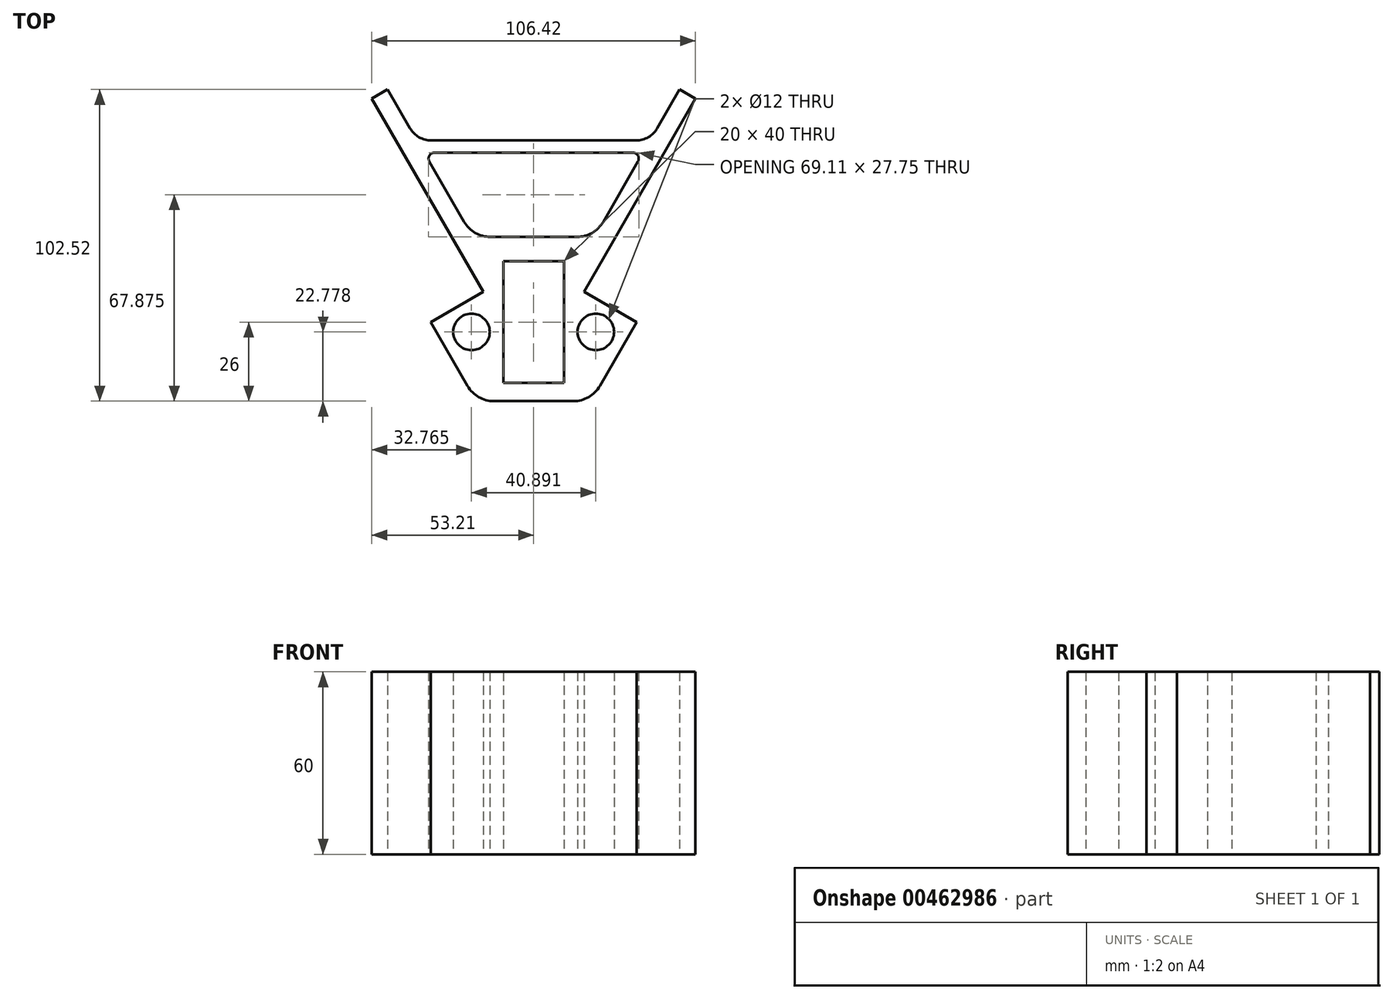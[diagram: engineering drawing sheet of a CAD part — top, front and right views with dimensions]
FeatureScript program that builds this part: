
annotation { "Feature Type Name" : "Feature", "Feature Type Description" : "" }
export const myFeature = defineFeature(function(context is Context, id is Id, definition is map)
    precondition{}
    {
        {
            var Q0;
            Q0=qCreatedBy(makeId("Top.planeOp"),FACE);
            var sketch = newSketch(context, id + "F0", { "sketchPlane" : qUnion([Q0])});
            skLineSegment(sketch, "E0.bottom", {"start": v(53.2, 49.76) * mm, "end": v(-53.2, 49.76) * mm, "construction": true});
            skLineSegment(sketch, "E0.top", {"start": v(53.2, -49.76) * mm, "end": v(-53.2, -49.76) * mm, "construction": true});
            skLineSegment(sketch, "E0.left", {"start": v(53.2, 49.76) * mm, "end": v(53.2, -49.76) * mm, "construction": true});
            skLineSegment(sketch, "E0.right", {"start": v(-53.2, 49.76) * mm, "end": v(-53.2, -49.76) * mm, "construction": true});
            skPoint(sketch, "E0.middle", {"position": v(0, 0) * mm});
            skLineSegment(sketch, "E1", {"start": v(-53.2, 49.76) * mm, "end": v(-16.53, -13.75) * mm});
            skLineSegment(sketch, "E2", {"start": v(53.2, 49.76) * mm, "end": v(16.54, -13.75) * mm});
            skLineSegment(sketch, "E3", {"start": v(-53.2, 49.76) * mm, "end": v(-48, 52.76) * mm});
            skLineSegment(sketch, "E4", {"start": v(-48, 52.76) * mm, "end": v(-40.64, 40) * mm});
            skLineSegment(sketch, "E5", {"start": v(53.2, 49.76) * mm, "end": v(48, 52.76) * mm});
            skLineSegment(sketch, "E6", {"start": v(48, 52.76) * mm, "end": v(40.64, 40) * mm});
            skLineSegment(sketch, "E7", {"start": v(16.54, -13.75) * mm, "end": v(33.86, -23.75) * mm});
            skLineSegment(sketch, "E8", {"start": v(33.86, -23.75) * mm, "end": v(21.73, -44.76) * mm});
            skLineSegment(sketch, "E9", {"start": v(-16.53, -13.75) * mm, "end": v(-33.86, -23.75) * mm});
            skLineSegment(sketch, "E10", {"start": v(-33.86, -23.75) * mm, "end": v(-21.73, -44.76) * mm});
            skLineSegment(sketch, "E11", {"start": v(-13.07, -49.76) * mm, "end": v(13.07, -49.76) * mm});
            skPoint(sketch, "E12.visualSharp", {"position": v(-18.84, -49.76) * mm});
            skArc(sketch, "E12.filletArc", {"start": v(-21.73, -44.76) * mm, "mid": v(-18.07, -48.42) * mm, "end": v(-13.07, -49.76) * mm});
            skPoint(sketch, "E13.visualSharp", {"position": v(18.84, -49.76) * mm});
            skArc(sketch, "E13.filletArc", {"start": v(13.07, -49.76) * mm, "mid": v(18.07, -48.42) * mm, "end": v(21.73, -44.76) * mm});
            skLineSegment(sketch, "E14.bottom", {"start": v(10, -43.76) * mm, "end": v(-10, -43.76) * mm});
            skLineSegment(sketch, "E14.top", {"start": v(10, -3.76) * mm, "end": v(-10, -3.76) * mm});
            skLineSegment(sketch, "E14.left", {"start": v(10, -43.76) * mm, "end": v(10, -3.76) * mm});
            skLineSegment(sketch, "E14.right", {"start": v(-10, -43.76) * mm, "end": v(-10, -3.76) * mm});
            skPoint(sketch, "E14.middle", {"position": v(0, -23.76) * mm});
            skLineSegment(sketch, "E15", {"start": v(14.22, 4.24) * mm, "end": v(-14.22, 4.24) * mm});
            skPoint(sketch, "E16.orphan", {"position": v(-19.1, 2.67) * mm});
            skPoint(sketch, "E17.orphan", {"position": v(19.1, 2.67) * mm});
            skPoint(sketch, "E18.visualSharp", {"position": v(-20, 4.24) * mm});
            skArc(sketch, "E18.filletArc", {"start": v(-22.88, 9.24) * mm, "mid": v(-19.22, 5.58) * mm, "end": v(-14.22, 4.24) * mm});
            skPoint(sketch, "E19.visualSharp", {"position": v(20, 4.24) * mm});
            skArc(sketch, "E19.filletArc", {"start": v(14.22, 4.24) * mm, "mid": v(19.22, 5.58) * mm, "end": v(22.88, 9.24) * mm});
            skLineSegment(sketch, "E20", {"start": v(32.55, 32) * mm, "end": v(-32.55, 31.99) * mm});
            skLineSegment(sketch, "E21", {"start": v(-33.7, 36) * mm, "end": v(33.7, 36) * mm});
            skLineSegment(sketch, "E22.trimOffspring", {"start": v(-34.29, 29) * mm, "end": v(-22.88, 9.24) * mm});
            skLineSegment(sketch, "E23.trimOffspring", {"start": v(34.29, 29) * mm, "end": v(22.88, 9.24) * mm});
            skPoint(sketch, "E24.visualSharp", {"position": v(-36.02, 31.99) * mm});
            skArc(sketch, "E24.filletArc", {"start": v(-32.55, 31.99) * mm, "mid": v(-34.29, 30.99) * mm, "end": v(-34.29, 28.99) * mm});
            skPoint(sketch, "E25.visualSharp", {"position": v(36.02, 32) * mm});
            skArc(sketch, "E25.filletArc", {"start": v(34.29, 29) * mm, "mid": v(34.29, 31) * mm, "end": v(32.55, 32) * mm});
            skPoint(sketch, "E26.visualSharp", {"position": v(-38.33, 36) * mm});
            skArc(sketch, "E26.filletArc", {"start": v(-40.64, 39.99) * mm, "mid": v(-37.7, 37.06) * mm, "end": v(-33.7, 36) * mm});
            skPoint(sketch, "E27.visualSharp", {"position": v(38.33, 36) * mm});
            skArc(sketch, "E27.filletArc", {"start": v(33.7, 36) * mm, "mid": v(37.7, 37.06) * mm, "end": v(40.64, 40) * mm});
            skLineSegment(sketch, "E28", {"start": v(-29.83, -10.72) * mm, "end": v(-15.63, -35.33) * mm, "construction": true});
            skLineSegment(sketch, "E29", {"start": v(28.86, -12.4) * mm, "end": v(15.63, -35.33) * mm, "construction": true});
            skCircle(sketch, "E30", {"center": v(-20.45, -26.98) * mm, "radius": 6 * mm});
            skCircle(sketch, "E31", {"center": v(20.45, -26.98) * mm, "radius": 6 * mm});
            skSolve(sketch);
        }
        {
            var Q0;
            Q0=qSketchRegion(id+"F0",true);
            extrude(context, id + "F1", {"entities" : qUnion([Q0]), "depth" : 60 * mm, "offsetDistance" : 25 * mm});
        }
    });
